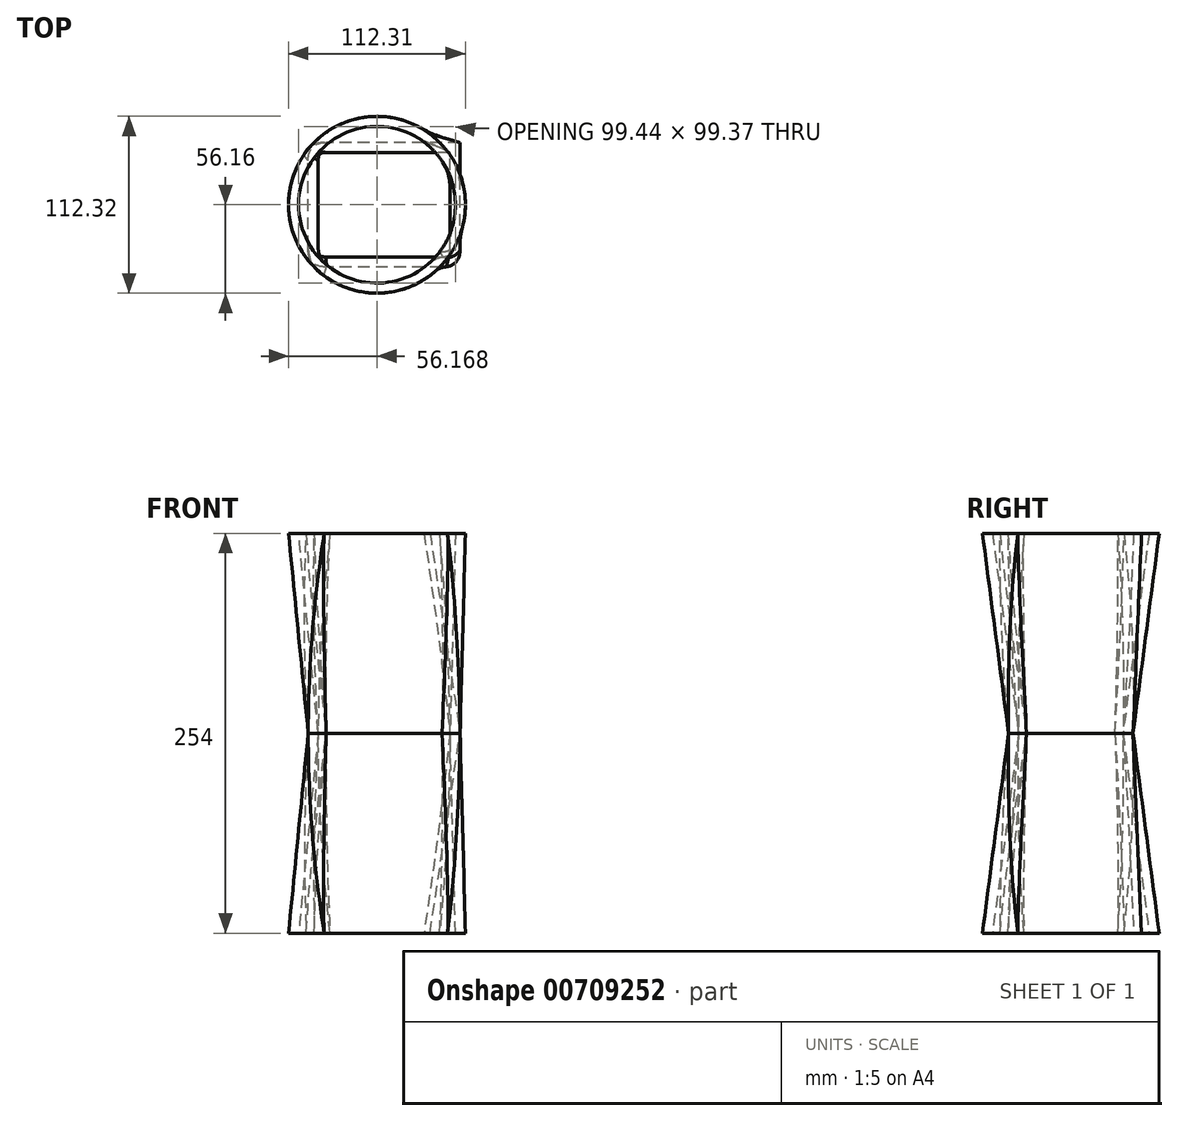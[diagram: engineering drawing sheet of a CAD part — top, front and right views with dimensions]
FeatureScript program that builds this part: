
annotation { "Feature Type Name" : "Feature", "Feature Type Description" : "" }
export const myFeature = defineFeature(function(context is Context, id is Id, definition is map)
    precondition{}
    {
        {
            var Q0;
            Q0=qCreatedBy(makeId("Top.planeOp"),FACE);
            var sketch = newSketch(context, id + "F0", { "sketchPlane" : qUnion([Q0])});
            skCircle(sketch, "E0", {"center": v(-4.53, 0) * mm, "radius": 56.16 * mm});
            skSolve(sketch);
        }
        {
            var Q0;
            Q0=qCreatedBy(makeId("Top.planeOp"),FACE);
            cPlane(context, id + "F1", {"entities" : qUnion([Q0]), "cplaneType" : CPlaneType.OFFSET, "offset" : 127 * mm, "width" : 152.4 * mm, "height" : 152.4 * mm});
        }
        {
            var Q0;
            Q0=qCreatedBy(id+"F1.planeOp",FACE);
            var sketch = newSketch(context, id + "F2", { "sketchPlane" : qUnion([Q0])});
            skLineSegment(sketch, "E1.bottom", {"start": v(48.23, -39.54) * mm, "end": v(-48.23, -39.54) * mm});
            skLineSegment(sketch, "E1.top", {"start": v(48.23, 39.54) * mm, "end": v(-48.23, 39.54) * mm});
            skLineSegment(sketch, "E1.left", {"start": v(48.23, -39.54) * mm, "end": v(48.23, 39.54) * mm});
            skLineSegment(sketch, "E1.right", {"start": v(-48.23, -39.54) * mm, "end": v(-48.23, 39.54) * mm});
            skPoint(sketch, "E1.middle", {"position": v(0, 0) * mm});
            skSolve(sketch);
        }
        {
            var Q0;
            Q0=makeQuery(id+"F0.imprint","IMPRINT",FACE,{"disambiguationData":[TD([[makeQuery(id+"F0.imprint","IMPRINT",EDGE,{"derivedFrom":sQuery(id+"F0.wireOp",EDGE,"E0")}),1.0]])]});
            var Q1;
            Q1=makeQuery(id+"F2.imprint","IMPRINT",FACE,{"disambiguationData":[TD([[makeQuery(id+"F2.imprint","IMPRINT",EDGE,{"derivedFrom":sQuery(id+"F2.wireOp",EDGE,"E1.bottom")}),-1.0]])]});
            loft(context, id + "F3", {"sheetProfilesArray" : [{ "sheetProfileEntities" : qUnion([Q0]) }, { "sheetProfileEntities" : qUnion([Q1]) }]});
        }
        {
            var Q0;
            Q0=makeQuery(id+"F3.opLoft","SWEPT_EDGE",EDGE,{"disambiguationData":[OSD([sQuery(id+"F2.wireOp",EDGE,"E1.bottom"),sQuery(id+"F2.wireOp",EDGE,"E1.left")])]});
            var Q1;
            Q1=makeQuery(id+"F3.opLoft","SWEPT_EDGE",EDGE,{"disambiguationData":[OSD([sQuery(id+"F0.wireOp",EDGE,"E0"),sQuery(id+"F2.wireOp",EDGE,"E1.bottom"),sQuery(id+"F2.wireOp",EDGE,"E1.top"),sQuery(id+"F2.wireOp",EDGE,"E1.left")])]});
            var Q2;
            Q2=makeQuery(id+"F3.opLoft","SWEPT_EDGE",EDGE,{"disambiguationData":[OSD([sQuery(id+"F0.wireOp",EDGE,"E0"),sQuery(id+"F2.wireOp",EDGE,"E1.bottom"),sQuery(id+"F2.wireOp",EDGE,"E1.top"),sQuery(id+"F2.wireOp",EDGE,"E1.right")])]});
            var Q3;
            Q3=makeQuery(id+"F3.opLoft","SWEPT_EDGE",EDGE,{"disambiguationData":[OSD([sQuery(id+"F0.wireOp",EDGE,"E0"),sQuery(id+"F2.wireOp",EDGE,"E1.top"),sQuery(id+"F2.wireOp",EDGE,"E1.left"),sQuery(id+"F2.wireOp",EDGE,"E1.right")])]});
            fillet(context, id + "F4", {"entities" : qUnion([Q0, Q1, Q2, Q3]), "radius" : 11.43 * mm, "tangentPropagation" : true, "rho" : 0.5, "crossSection" : FilletCrossSection.CONIC, "allowEdgeOverflow" : false});
        }
        {
            var Q0;
            Q0=makeQuery(id+"F3.opLoft","CAP_FACE",FACE,{"disambiguationData":[OSD([makeQuery(id+"F2.imprint","IMPRINT",FACE,{"disambiguationData":[TD([[makeQuery(id+"F2.imprint","IMPRINT",EDGE,{"derivedFrom":sQuery(id+"F2.wireOp",EDGE,"E1.bottom")}),-1.0]])]})])],"isStart":true});
            var Q1;
            Q1=makeQuery(id+"F3.opLoft","CAP_FACE",FACE,{"disambiguationData":[OSD([makeQuery(id+"F0.imprint","IMPRINT",FACE,{"disambiguationData":[TD([[makeQuery(id+"F0.imprint","IMPRINT",EDGE,{"derivedFrom":sQuery(id+"F0.wireOp",EDGE,"E0")}),1.0]])]})])],"isStart":true});
            shell(context, id + "F5", {"entities" : qUnion([Q0, Q1]), "thickness" : 6.35 * mm});
        }
        {
            var Q0;
            Q0=makeQuery(id+"F3.opLoft","SWEPT_BODY",BODY,{"disambiguationData":[OSD([makeQuery(id+"F0.imprint","IMPRINT",FACE,{"disambiguationData":[TD([[makeQuery(id+"F0.imprint","IMPRINT",EDGE,{"derivedFrom":sQuery(id+"F0.wireOp",EDGE,"E0")}),1.0]])]}),makeQuery(id+"F2.imprint","IMPRINT",FACE,{"disambiguationData":[TD([[makeQuery(id+"F2.imprint","IMPRINT",EDGE,{"derivedFrom":sQuery(id+"F2.wireOp",EDGE,"E1.bottom")}),-1.0]])]})])]});
            var Q1;
            Q1=makeQuery(id+"F3.opLoft","CAP_FACE",FACE,{"disambiguationData":[OSD([makeQuery(id+"F2.imprint","IMPRINT",FACE,{"disambiguationData":[TD([[makeQuery(id+"F2.imprint","IMPRINT",EDGE,{"derivedFrom":sQuery(id+"F2.wireOp",EDGE,"E1.bottom")}),-1.0]])]})])],"isStart":true});
            mirror(context, id + "F6", {"operationType" : NewBodyOperationType.ADD, "entities" : qUnion([Q0]), "mirrorPlane" : qUnion([Q1])});
        }
    });
